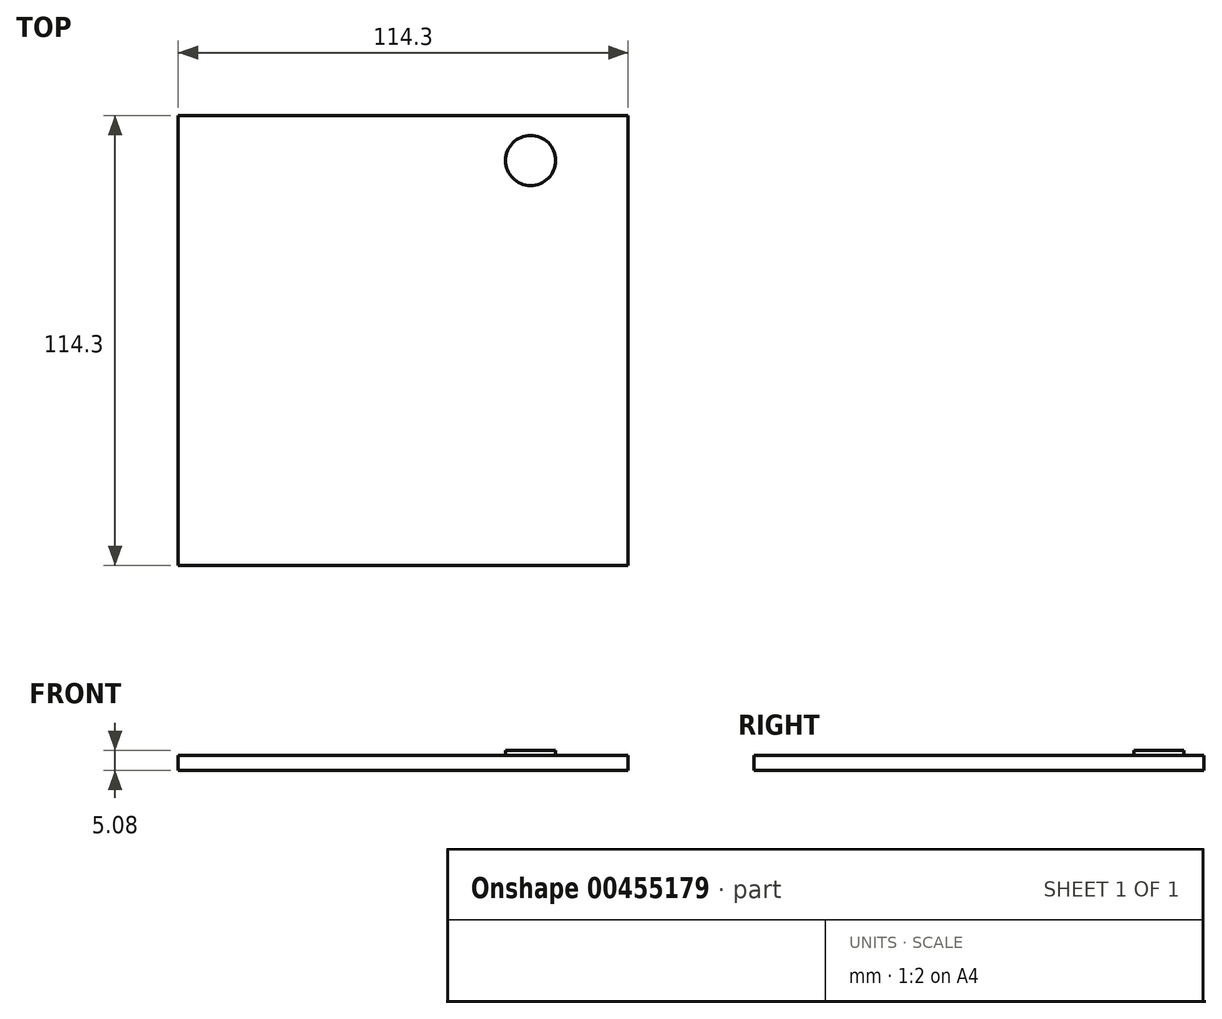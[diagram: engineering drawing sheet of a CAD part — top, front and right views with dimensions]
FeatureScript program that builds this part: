
annotation { "Feature Type Name" : "Feature", "Feature Type Description" : "" }
export const myFeature = defineFeature(function(context is Context, id is Id, definition is map)
    precondition{}
    {
        {
            var Q0;
            Q0=qCreatedBy(makeId("Top.planeOp"),FACE);
            var sketch = newSketch(context, id + "F0", { "sketchPlane" : qUnion([Q0])});
            skLineSegment(sketch, "E0.bottom", {"start": v(57.15, 57.15) * mm, "end": v(-57.15, 57.15) * mm});
            skLineSegment(sketch, "E0.top", {"start": v(57.15, -57.15) * mm, "end": v(-57.15, -57.15) * mm});
            skLineSegment(sketch, "E0.left", {"start": v(57.15, 57.15) * mm, "end": v(57.15, -57.15) * mm});
            skLineSegment(sketch, "E0.right", {"start": v(-57.15, 57.15) * mm, "end": v(-57.15, -57.15) * mm});
            skPoint(sketch, "E0.middle", {"position": v(0, 0) * mm});
            skSolve(sketch);
        }
        {
            var Q0;
            Q0=makeQuery(id+"F0.imprint","IMPRINT",FACE,{"disambiguationData":[TD([[makeQuery(id+"F0.imprint","IMPRINT",EDGE,{"derivedFrom":sQuery(id+"F0.wireOp",EDGE,"E0.bottom")}),1.0]])]});
            extrude(context, id + "F1", {"entities" : qUnion([Q0]), "depth" : 2.54 * mm});
        }
        {
            var Q0;
            Q0=makeQuery(id+"F1.opExtrude","SWEPT_FACE",FACE,{"disambiguationData":[OSD([sQuery(id+"F0.wireOp",EDGE,"E0.left")])]});
            var sketch = newSketch(context, id + "F2", { "sketchPlane" : qUnion([Q0])});
            skLineSegment(sketch, "E1.bottom", {"start": v(-57.15, 0) * mm, "end": v(57.15, 0) * mm});
            skLineSegment(sketch, "E2.top", {"start": v(-57.15, 27.94) * mm, "end": v(57.15, 27.94) * mm});
            skLineSegment(sketch, "E2.left", {"start": v(-57.15, 2.54) * mm, "end": v(-57.15, 27.94) * mm});
            skLineSegment(sketch, "E2.right", {"start": v(57.15, 2.54) * mm, "end": v(57.15, 27.94) * mm});
            skSolve(sketch);
        }
        {
            var Q0;
            Q0=makeQuery(id+"F2.imprint","IMPRINT",FACE,{"disambiguationData":[TD([[makeQuery(id+"F2.imprint","IMPRINT",EDGE,{"derivedFrom":sQuery(id+"F2.wireOp",EDGE,"E2.top")}),-1.0]])]});
            extrude(context, id + "F3", {"entities" : qUnion([Q0]), "oppositeDirection" : true, "depth" : 2.54 * mm});
        }
        {
            var Q0;
            Q0=makeQuery(id+"F3.opExtrude","SWEPT_BODY",BODY,{"disambiguationData":[OSD([sQuery(id+"F0.wireOp",EDGE,"E0.left"),sQuery(id+"F2.wireOp",EDGE,"E2.top"),sQuery(id+"F2.wireOp",EDGE,"E2.left"),sQuery(id+"F2.wireOp",EDGE,"E2.right")])]});
            var Q1;
            Q1=qCreatedBy(makeId("Right.planeOp"),FACE);
            mirror(context, id + "F4", {"operationType" : NewBodyOperationType.ADD, "entities" : qUnion([Q0]), "mirrorPlane" : qUnion([Q1])});
        }
        {
            var Q0;
            {var subQ0=makeQuery(id+"F3.opExtrude","SWEPT_FACE",FACE,{"disambiguationData":[OSD([sQuery(id+"F2.wireOp",EDGE,"E2.right")])]});Q0=makeQuery(id+"F4.boolean.opBoolean","MERGE",FACE,{"derivedFrom":[makeQuery(id+"F1.opExtrude","SWEPT_FACE",FACE,{"disambiguationData":[OSD([sQuery(id+"F0.wireOp",EDGE,"E0.bottom")])]}),subQ0,makeQuery(id+"F4.opPattern","COPY",FACE,{"derivedFrom":subQ0,"instanceName":"1"})]});}
            var sketch = newSketch(context, id + "F5", { "sketchPlane" : qUnion([Q0])});
            skLineSegment(sketch, "E3.bottom", {"start": v(-54.61, 2.54) * mm, "end": v(54.61, 2.54) * mm});
            skLineSegment(sketch, "E3.top", {"start": v(-54.61, 27.94) * mm, "end": v(54.61, 27.94) * mm});
            skLineSegment(sketch, "E3.left", {"start": v(-54.61, 2.54) * mm, "end": v(-54.61, 27.94) * mm});
            skLineSegment(sketch, "E3.right", {"start": v(54.61, 2.54) * mm, "end": v(54.61, 27.94) * mm});
            skSolve(sketch);
        }
        {
            var Q0;
            Q0=makeQuery(id+"F5.imprint","IMPRINT",FACE,{"disambiguationData":[TD([[makeQuery(id+"F5.imprint","IMPRINT",EDGE,{"derivedFrom":sQuery(id+"F5.wireOp",EDGE,"E3.bottom")}),1.0]])]});
            extrude(context, id + "F6", {"entities" : qUnion([Q0]), "oppositeDirection" : true, "depth" : 2.54 * mm});
        }
        {
            var Q0;
            Q0=makeQuery(id+"F6.opExtrude","SWEPT_BODY",BODY,{"disambiguationData":[OSD([sQuery(id+"F5.wireOp",EDGE,"E3.bottom"),sQuery(id+"F5.wireOp",EDGE,"E3.top"),sQuery(id+"F5.wireOp",EDGE,"E3.left"),sQuery(id+"F5.wireOp",EDGE,"E3.right")])]});
            var Q1;
            Q1=qCreatedBy(makeId("Front.planeOp"),FACE);
            mirror(context, id + "F7", {"operationType" : NewBodyOperationType.ADD, "entities" : qUnion([Q0]), "mirrorPlane" : qUnion([Q1])});
        }
        {
            var Q0;
            {var subQ0=makeQuery(id+"F6.opExtrude","SWEPT_FACE",FACE,{"disambiguationData":[OSD([sQuery(id+"F5.wireOp",EDGE,"E3.top")])]});var subQ1=makeQuery(id+"F3.opExtrude","SWEPT_FACE",FACE,{"disambiguationData":[OSD([sQuery(id+"F2.wireOp",EDGE,"E2.top")])]});Q0=makeQuery(id+"F7.boolean.opBoolean","MERGE",FACE,{"derivedFrom":[subQ1,makeQuery(id+"F4.opPattern","COPY",FACE,{"derivedFrom":subQ1,"instanceName":"1"}),subQ0,makeQuery(id+"F7.opPattern","COPY",FACE,{"derivedFrom":subQ0,"instanceName":"1"})]});}
            var sketch = newSketch(context, id + "F8", { "sketchPlane" : qUnion([Q0])});
            skLineSegment(sketch, "E4.bottom", {"start": v(57.15, 57.15) * mm, "end": v(-57.15, 57.15) * mm});
            skLineSegment(sketch, "E4.top", {"start": v(57.15, -57.15) * mm, "end": v(-57.15, -57.15) * mm});
            skLineSegment(sketch, "E4.left", {"start": v(57.15, 57.15) * mm, "end": v(57.15, -57.15) * mm});
            skLineSegment(sketch, "E4.right", {"start": v(-57.15, 57.15) * mm, "end": v(-57.15, -57.15) * mm});
            skSolve(sketch);
        }
        {
            var Q0;
            Q0=makeQuery(id+"F8.imprint","IMPRINT",FACE,{"disambiguationData":[TD([[makeQuery(id+"F8.imprint","IMPRINT",EDGE,{"derivedFrom":sQuery(id+"F8.wireOp",EDGE,"E4.bottom")}),-1.0]])]});
            var Q1;
            {var subQ0=makeQuery(id+"F6.opExtrude","CAP_EDGE",EDGE,{"disambiguationData":[OSD([sQuery(id+"F5.wireOp",EDGE,"E3.top")])],"isStart":false});Q1=makeQuery(id+"F8.imprint","IMPRINT",FACE,{"disambiguationData":[TD([[makeQuery(id+"F8.imprint","IMPRINT",EDGE,{"derivedFrom":subQ0}),1.0]])]});}
            extrude(context, id + "F9", {"entities" : qUnion([Q0, Q1]), "depth" : 2.54 * mm});
        }
        {
            var Q0;
            Q0=makeQuery(id+"F9.opExtrude","CAP_FACE",FACE,{"disambiguationData":[OSD([sQuery(id+"F8.wireOp",EDGE,"E4.bottom"),sQuery(id+"F8.wireOp",EDGE,"E4.top"),sQuery(id+"F8.wireOp",EDGE,"E4.left"),sQuery(id+"F8.wireOp",EDGE,"E4.right")])],"isStart":false});
            var sketch = newSketch(context, id + "F10", { "sketchPlane" : qUnion([Q0])});
            skLineSegment(sketch, "E5.bottom", {"start": v(57.15, 57.15) * mm, "end": v(-57.15, 57.15) * mm});
            skLineSegment(sketch, "E5.top", {"start": v(57.15, -57.15) * mm, "end": v(-57.15, -57.15) * mm});
            skLineSegment(sketch, "E5.left", {"start": v(57.15, 57.15) * mm, "end": v(57.15, -57.15) * mm});
            skLineSegment(sketch, "E5.right", {"start": v(-57.15, 57.15) * mm, "end": v(-57.15, -57.15) * mm});
            skSolve(sketch);
        }
        {
            var Q0;
            Q0=makeQuery(id+"F10.imprint","IMPRINT",FACE,{"disambiguationData":[TD([[makeQuery(id+"F10.imprint","IMPRINT",EDGE,{"derivedFrom":sQuery(id+"F10.wireOp",EDGE,"E5.bottom")}),-1.0]])]});
            extrude(context, id + "F11", {"entities" : qUnion([Q0]), "operationType" : NewBodyOperationType.ADD, "depth" : 2.54 * mm});
        }
        {
            var Q0;
            Q0=makeQuery(id+"F11.opExtrude","CAP_FACE",FACE,{"disambiguationData":[OSD([sQuery(id+"F10.wireOp",EDGE,"E5.bottom"),sQuery(id+"F10.wireOp",EDGE,"E5.top"),sQuery(id+"F10.wireOp",EDGE,"E5.left"),sQuery(id+"F10.wireOp",EDGE,"E5.right")])],"isStart":false});
            var sketch = newSketch(context, id + "F12", { "sketchPlane" : qUnion([Q0])});
            skLineSegment(sketch, "E6.bottom", {"start": v(-57.15, 57.15) * mm, "end": v(-52.07, 57.15) * mm});
            skLineSegment(sketch, "E6.top", {"start": v(-57.15, 52.07) * mm, "end": v(-52.07, 52.07) * mm});
            skLineSegment(sketch, "E6.left", {"start": v(-57.15, 57.15) * mm, "end": v(-57.15, 52.07) * mm});
            skLineSegment(sketch, "E6.right", {"start": v(-52.07, 57.15) * mm, "end": v(-52.07, 52.07) * mm});
            skLineSegment(sketch, "E7.bottom", {"start": v(-52.07, 52.07) * mm, "end": v(24.13, 52.07) * mm});
            skLineSegment(sketch, "E7.top", {"start": v(-52.07, -52.07) * mm, "end": v(24.13, -52.07) * mm});
            skLineSegment(sketch, "E7.left", {"start": v(-52.07, 52.07) * mm, "end": v(-52.07, -52.07) * mm});
            skLineSegment(sketch, "E7.right", {"start": v(24.13, 52.07) * mm, "end": v(24.13, -52.07) * mm});
            skSolve(sketch);
        }
        {
            var Q0;
            Q0=makeQuery(id+"F12.imprint","IMPRINT",FACE,{"disambiguationData":[TD([[makeQuery(id+"F12.imprint","IMPRINT",EDGE,{"derivedFrom":sQuery(id+"F12.wireOp",EDGE,"E7.bottom")}),-1.0]])]});
            extrude(context, id + "F13", {"entities" : qUnion([Q0]), "operationType" : NewBodyOperationType.REMOVE, "oppositeDirection" : true, "depth" : 1.27 * mm});
        }
        {
            var Q0;
            Q0=makeQuery(id+"F11.opExtrude","CAP_FACE",FACE,{"disambiguationData":[OSD([sQuery(id+"F10.wireOp",EDGE,"E5.bottom"),sQuery(id+"F10.wireOp",EDGE,"E5.top"),sQuery(id+"F10.wireOp",EDGE,"E5.left"),sQuery(id+"F10.wireOp",EDGE,"E5.right")])],"isStart":false});
            var sketch = newSketch(context, id + "F14", { "sketchPlane" : qUnion([Q0])});
            skLineSegment(sketch, "E8", {"start": v(0, 0) * mm, "end": v(40.64, 0) * mm, "construction": true});
            skPoint(sketch, "E8.endSnap0", {"position": v(24.13, 0) * mm});
            skCircle(sketch, "E9", {"center": v(40.64, 0) * mm, "radius": 6.35 * mm});
            skLineSegment(sketch, "E10", {"start": v(40.64, 0) * mm, "end": v(40.64, 45.72) * mm});
            skLineSegment(sketch, "E11", {"start": v(40.64, 45.72) * mm, "end": v(48.9, 45.72) * mm});
            skCircle(sketch, "E12", {"center": v(48.9, 45.72) * mm, "radius": 6.35 * mm});
            skCircle(sketch, "E13.MirrorC", {"center": v(32.39, 45.72) * mm, "radius": 6.35 * mm});
            skSolve(sketch);
        }
        {
            var Q0;
            Q0=makeQuery(id+"F14.imprint","IMPRINT",FACE,{"disambiguationData":[TD([[makeQuery(id+"F14.imprint","IMPRINT",EDGE,{"derivedFrom":sQuery(id+"F14.wireOp",EDGE,"E12")}),1.0]])]});
            var Q1;
            Q1=makeQuery(id+"F14.imprint","IMPRINT",FACE,{"disambiguationData":[TD([[makeQuery(id+"F14.imprint","IMPRINT",EDGE,{"derivedFrom":sQuery(id+"F14.wireOp",EDGE,"E13.MirrorC")}),-1.0]])]});
            var Q2;
            Q2=makeQuery(id+"F14.imprint","IMPRINT",FACE,{"disambiguationData":[TD([[makeQuery(id+"F14.imprint","IMPRINT",EDGE,{"derivedFrom":sQuery(id+"F14.wireOp",EDGE,"E9")}),1.0]])]});
            extrude(context, id + "F15", {"entities" : qUnion([Q0, Q1, Q2]), "operationType" : NewBodyOperationType.REMOVE, "oppositeDirection" : true, "depth" : 1.27 * mm});
        }
        {
            var Q0;
            Q0=makeQuery(id+"F1.opExtrude","SWEPT_BODY",BODY,{"disambiguationData":[OSD([sQuery(id+"F0.wireOp",EDGE,"E0.bottom"),sQuery(id+"F0.wireOp",EDGE,"E0.top"),sQuery(id+"F0.wireOp",EDGE,"E0.left"),sQuery(id+"F0.wireOp",EDGE,"E0.right")])]});
            deleteBodies(context, id + "F16", {"entities" : qUnion([Q0])});
        }
        {
            var Q0;
            Q0=makeQuery(id+"F9.opExtrude","CAP_FACE",FACE,{"disambiguationData":[OSD([sQuery(id+"F8.wireOp",EDGE,"E4.bottom"),sQuery(id+"F8.wireOp",EDGE,"E4.top"),sQuery(id+"F8.wireOp",EDGE,"E4.left"),sQuery(id+"F8.wireOp",EDGE,"E4.right")])],"isStart":true});
            var sketch = newSketch(context, id + "F17", { "sketchPlane" : qUnion([Q0])});
            skLineSegment(sketch, "E14.bottom", {"start": v(55.63, 55.63) * mm, "end": v(-55.63, 55.63) * mm});
            skLineSegment(sketch, "E14.top", {"start": v(55.63, -55.63) * mm, "end": v(-55.63, -55.63) * mm});
            skLineSegment(sketch, "E14.left", {"start": v(55.63, 55.63) * mm, "end": v(55.63, -55.63) * mm});
            skLineSegment(sketch, "E14.right", {"start": v(-55.63, 55.63) * mm, "end": v(-55.63, -55.63) * mm});
            skPoint(sketch, "E14.middle", {"position": v(0, 0) * mm});
            skSolve(sketch);
        }
        {
            var Q0;
            Q0=makeQuery(id+"F17.imprint","IMPRINT",FACE,{"disambiguationData":[TD([[makeQuery(id+"F17.imprint","IMPRINT",EDGE,{"derivedFrom":sQuery(id+"F17.wireOp",EDGE,"E14.bottom")}),1.0]])]});
            extrude(context, id + "F18", {"entities" : qUnion([Q0]), "depth" : 1.9 * mm});
        }
        {
            var Q0;
            Q0=makeQuery(id+"F18.opExtrude","SWEPT_BODY",BODY,{"disambiguationData":[OSD([sQuery(id+"F17.wireOp",EDGE,"E14.bottom"),sQuery(id+"F17.wireOp",EDGE,"E14.top"),sQuery(id+"F17.wireOp",EDGE,"E14.left"),sQuery(id+"F17.wireOp",EDGE,"E14.right")])]});
            deleteBodies(context, id + "F19", {"entities" : qUnion([Q0])});
        }
    });
